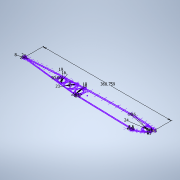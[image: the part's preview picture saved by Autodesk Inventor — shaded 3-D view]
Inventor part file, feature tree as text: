
AUTODESK INVENTOR PART (.ipt)
format: ipt  version: 2022 (Build 260153000, 153)  size: 232,960 bytes
history: native  units: mm
features: sketch x1
ambient origin geometry x8: Origin, YZ Plane, XZ Plane, XY Plane, X Axis, Y Axis, Z Axis, Center Point
feature tree (1):
  sketch  "Sketch1"  dims[d31=34.456mm d50=368.759386mm d57=16.0mm d69=8.0mm d70=23.0mm d71=8.0mm d73=16.0mm d80=19.0mm d81=16.0mm d82=1.0mm d83=1.0mm d84=1.0mm d85=1.0mm d86=1.0mm d87=0.8mm d88=1.0mm d90=19.0mm d94=5.0mm d95=5.0mm d105=5.0mm d106=5.0mm d108=2.0mm d109=19.0mm d114=5.0mm d115=5.0mm d116=24.0mm d117=2.5mm d118=2.5mm d123=2.5mm d124=2.5mm d125=10.0mm d126=24.0mm d127=24.0mm d128=27.0mm d130=90.0deg]
